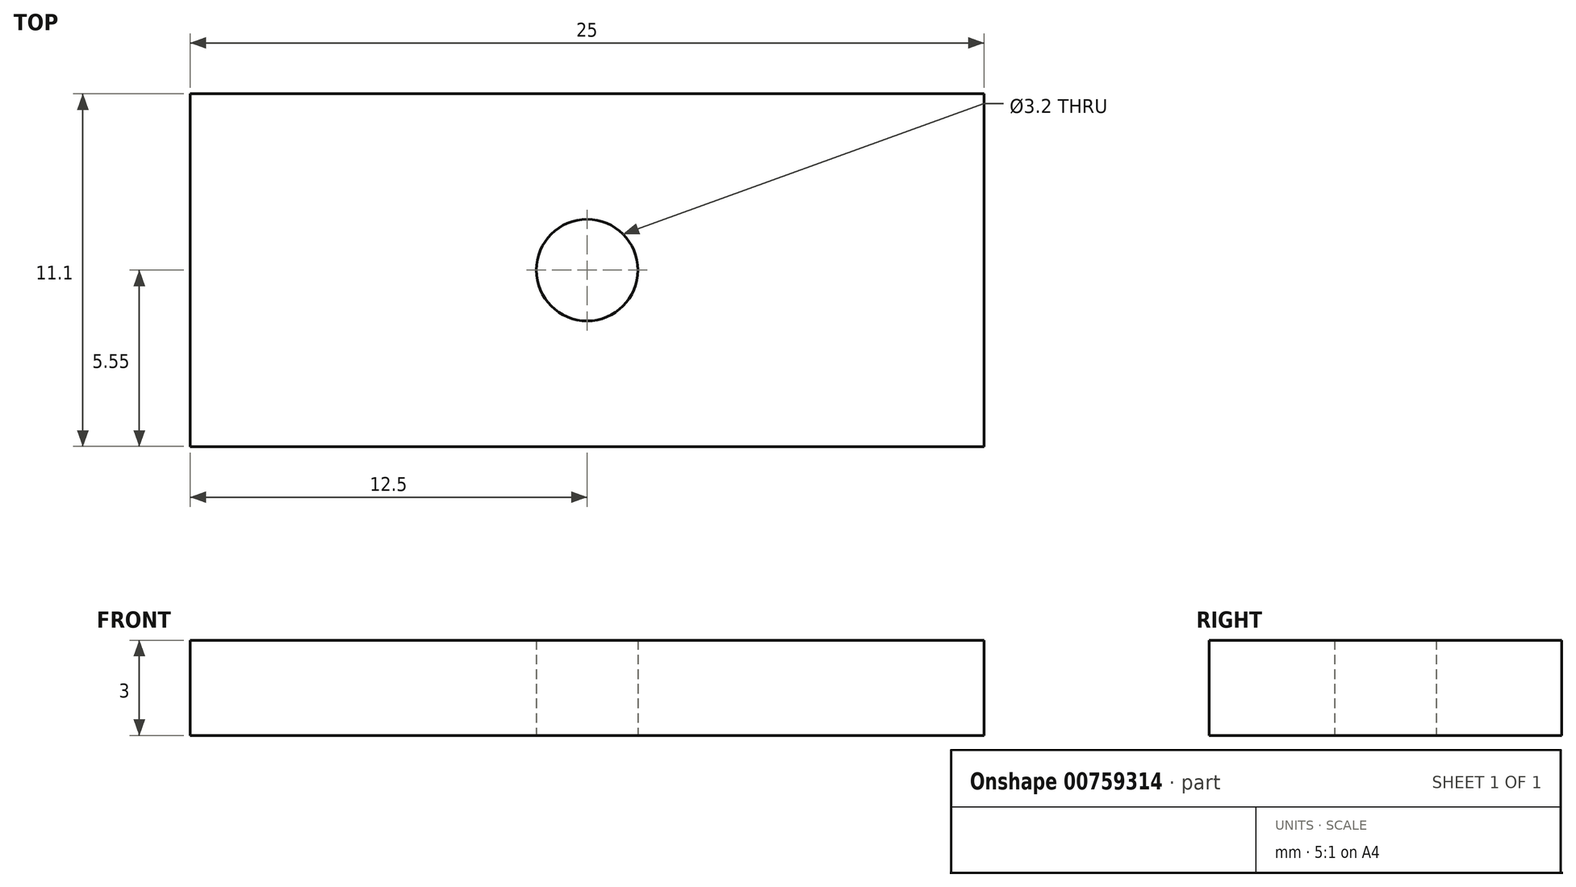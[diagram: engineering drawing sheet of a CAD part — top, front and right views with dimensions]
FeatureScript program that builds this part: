
annotation { "Feature Type Name" : "Feature", "Feature Type Description" : "" }
export const myFeature = defineFeature(function(context is Context, id is Id, definition is map)
    precondition{}
    {
        {
            var Q0;
            Q0=qCreatedBy(makeId("Top.planeOp"),FACE);
            var sketch = newSketch(context, id + "F0", { "sketchPlane" : qUnion([Q0])});
            skLineSegment(sketch, "E0.bottom", {"start": v(-12.5, 5.56) * mm, "end": v(12.5, 5.56) * mm});
            skLineSegment(sketch, "E0.top", {"start": v(-12.5, -5.55) * mm, "end": v(12.5, -5.55) * mm});
            skLineSegment(sketch, "E0.left", {"start": v(-12.5, 5.55) * mm, "end": v(-12.5, -5.55) * mm});
            skLineSegment(sketch, "E0.right", {"start": v(12.5, 5.56) * mm, "end": v(12.5, -5.55) * mm});
            skPoint(sketch, "E0.middle", {"position": v(0, 0) * mm});
            skCircle(sketch, "E1", {"center": v(0, 0) * mm, "radius": 1.6 * mm});
            skSolve(sketch);
        }
        {
            var Q0;
            Q0=makeQuery(id+"F0.imprint","IMPRINT",FACE,{"disambiguationData":[TD([[makeQuery(id+"F0.imprint","IMPRINT",EDGE,{"derivedFrom":sQuery(id+"F0.wireOp",EDGE,"E0.bottom")}),-1.0]])]});
            extrude(context, id + "F1", {"entities" : qUnion([Q0]), "depth" : 3 * mm, "offsetDistance" : 25 * mm});
        }
    });
